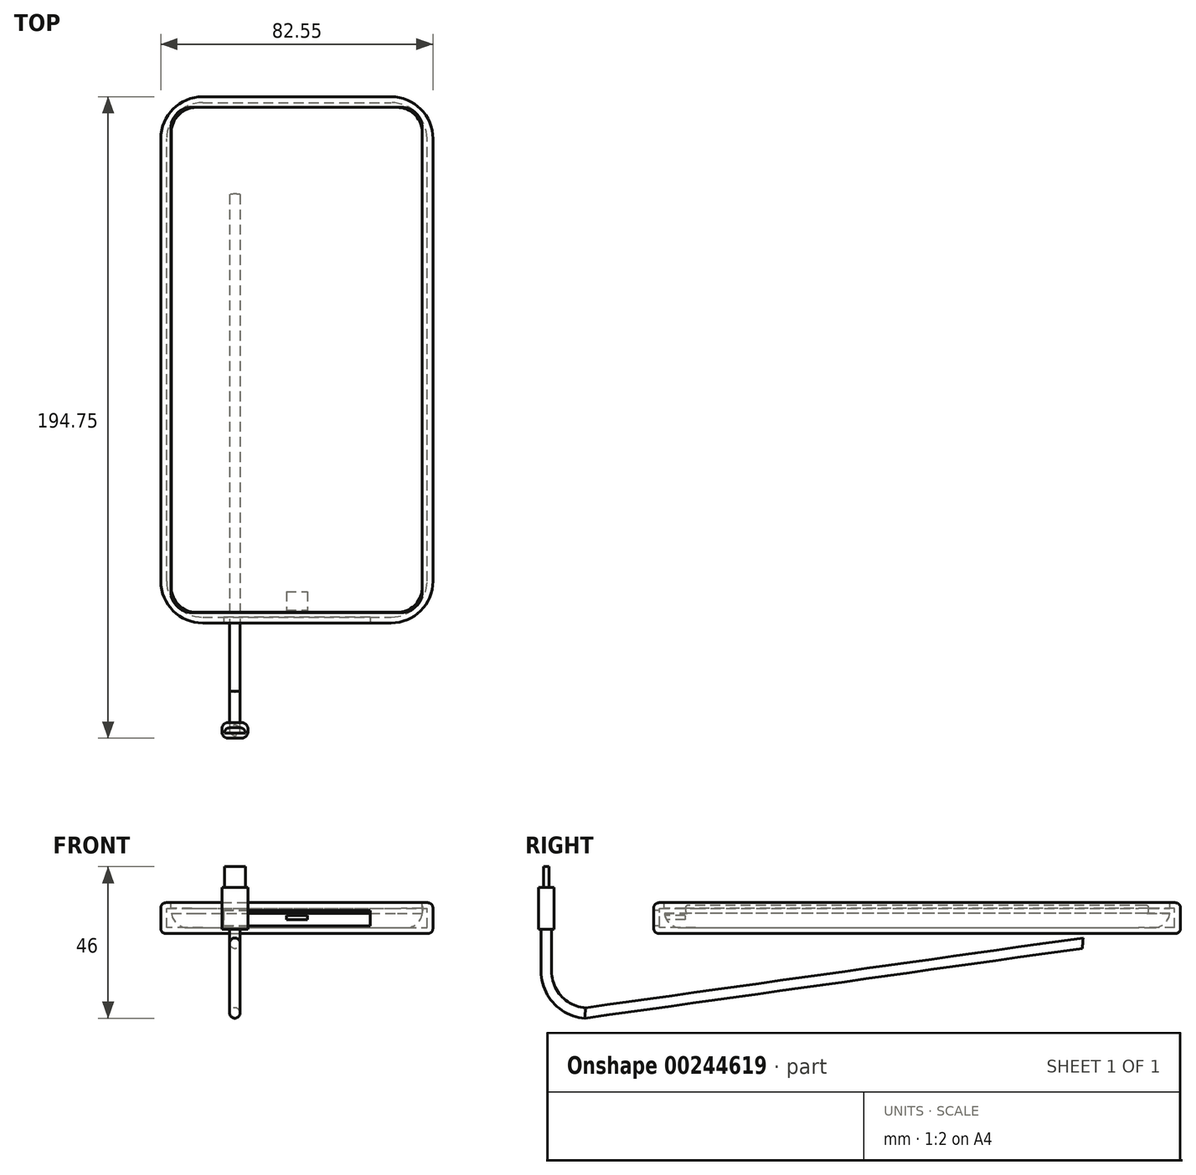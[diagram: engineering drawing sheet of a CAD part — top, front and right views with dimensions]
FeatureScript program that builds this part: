
annotation { "Feature Type Name" : "Feature", "Feature Type Description" : "" }
export const myFeature = defineFeature(function(context is Context, id is Id, definition is map)
    precondition{}
    {
        {
            var Q0;
            Q0=qCreatedBy(makeId("Top.planeOp"),FACE);
            var sketch = newSketch(context, id + "F0", { "sketchPlane" : qUnion([Q0])});
            skLineSegment(sketch, "E0.bottom", {"start": v(-19.3, -23.27) * mm, "end": v(56.9, -23.27) * mm});
            skLineSegment(sketch, "E0.top", {"start": v(-19.3, 130.15) * mm, "end": v(56.9, 130.15) * mm});
            skLineSegment(sketch, "E0.left", {"start": v(-19.3, -23.27) * mm, "end": v(-19.3, 130.15) * mm});
            skLineSegment(sketch, "E0.right", {"start": v(56.9, -23.27) * mm, "end": v(56.9, 130.15) * mm});
            skSolve(sketch);
        }
        {
            var Q0;
            Q0=makeQuery(id+"F0.imprint","IMPRINT",FACE,{"disambiguationData":[TD([[makeQuery(id+"F0.imprint","IMPRINT",EDGE,{"derivedFrom":sQuery(id+"F0.wireOp",EDGE,"E0.bottom")}),1.0]])]});
            extrude(context, id + "F1", {"entities" : qUnion([Q0]), "depth" : 7.62 * mm});
        }
        {
            var Q0;
            Q0=makeQuery(id+"F1.opExtrude","SWEPT_EDGE",EDGE,{"disambiguationData":[OSD([sQuery(id+"F0.wireOp",EDGE,"E0.bottom"),sQuery(id+"F0.wireOp",EDGE,"E0.left")])]});
            var Q1;
            Q1=makeQuery(id+"F1.opExtrude","SWEPT_EDGE",EDGE,{"disambiguationData":[OSD([sQuery(id+"F0.wireOp",EDGE,"E0.top"),sQuery(id+"F0.wireOp",EDGE,"E0.left")])]});
            var Q2;
            Q2=makeQuery(id+"F1.opExtrude","SWEPT_EDGE",EDGE,{"disambiguationData":[OSD([sQuery(id+"F0.wireOp",EDGE,"E0.top"),sQuery(id+"F0.wireOp",EDGE,"E0.right")])]});
            var Q3;
            Q3=makeQuery(id+"F1.opExtrude","SWEPT_EDGE",EDGE,{"disambiguationData":[OSD([sQuery(id+"F0.wireOp",EDGE,"E0.bottom"),sQuery(id+"F0.wireOp",EDGE,"E0.right")])]});
            fillet(context, id + "F2", {"entities" : qUnion([Q0, Q1, Q2, Q3]), "radius" : 7.62 * mm, "tangentPropagation" : true, "allowEdgeOverflow" : false});
        }
        {
            var Q0;
            Q0=makeQuery(id+"F1.opExtrude","CAP_EDGE",EDGE,{"disambiguationData":[OSD([sQuery(id+"F0.wireOp",EDGE,"E0.top")])],"isStart":true});
            var Q1;
            Q1=makeQuery(id+"F1.opExtrude","CAP_FACE",FACE,{"disambiguationData":[OSD([sQuery(id+"F0.wireOp",EDGE,"E0.bottom"),sQuery(id+"F0.wireOp",EDGE,"E0.top"),sQuery(id+"F0.wireOp",EDGE,"E0.left"),sQuery(id+"F0.wireOp",EDGE,"E0.right")])],"isStart":true});
            fillet(context, id + "F3", {"entities" : qUnion([Q0, Q1]), "radius" : 5.08 * mm, "tangentPropagation" : true, "allowEdgeOverflow" : false});
        }
        {
            var Q0;
            Q0=makeQuery(id+"F1.opExtrude","CAP_EDGE",EDGE,{"disambiguationData":[OSD([sQuery(id+"F0.wireOp",EDGE,"E0.top")])],"isStart":false});
            fillet(context, id + "F4", {"entities" : qUnion([Q0]), "radius" : 1.27 * mm, "tangentPropagation" : true, "allowEdgeOverflow" : false});
        }
        {
            var Q0;
            Q0=makeQuery(id+"F1.opExtrude","SWEPT_FACE",FACE,{"disambiguationData":[OSD([sQuery(id+"F0.wireOp",EDGE,"E0.bottom")])]});
            var sketch = newSketch(context, id + "F5", { "sketchPlane" : qUnion([Q0])});
            skLineSegment(sketch, "E1.bottom", {"start": v(15.62, 3.76) * mm, "end": v(21.97, 3.76) * mm});
            skLineSegment(sketch, "E1.top", {"start": v(15.62, 2.49) * mm, "end": v(21.97, 2.49) * mm});
            skLineSegment(sketch, "E1.left", {"start": v(15.62, 3.76) * mm, "end": v(15.62, 2.49) * mm});
            skLineSegment(sketch, "E1.right", {"start": v(21.97, 3.76) * mm, "end": v(21.97, 2.49) * mm});
            skSolve(sketch);
        }
        {
            var Q0;
            Q0=makeQuery(id+"F5.imprint","IMPRINT",FACE,{"disambiguationData":[TD([[makeQuery(id+"F5.imprint","IMPRINT",EDGE,{"derivedFrom":sQuery(id+"F5.wireOp",EDGE,"E1.bottom")}),-1.0]])]});
            extrude(context, id + "F6", {"entities" : qUnion([Q0]), "operationType" : NewBodyOperationType.REMOVE, "oppositeDirection" : true, "depth" : 6.35 * mm});
        }
        {
            var Q0;
            Q0=qCreatedBy(makeId("Right.planeOp"),FACE);
            var sketch = newSketch(context, id + "F7", { "sketchPlane" : qUnion([Q0])});
            skLineSegment(sketch, "E2", {"start": v(-59.05, -0.5) * mm, "end": v(-59.05, -13.2) * mm});
            skArc(sketch, "E3", {"start": v(-59.05, -13.2) * mm, "mid": v(-55.64, -21.86) * mm, "end": v(-47.24, -25.87) * mm});
            skLineSegment(sketch, "E4", {"start": v(-47.24, -25.87) * mm, "end": v(103.67, -4.66) * mm});
            skSolve(sketch);
        }
        {
            var Q0;
            Q0=sQuery(id+"F7.wireOp",VERTEX,"E2.start");
            var Q1;
            Q1=qCreatedBy(makeId("Top.planeOp"),FACE);
            cPlane(context, id + "F8", {"entities" : qUnion([Q0, Q1]), "cplaneType" : CPlaneType.PLANE_POINT, "offset" : 25.4 * mm, "width" : 152.4 * mm, "height" : 152.4 * mm});
        }
        {
            var Q0;
            Q0=qCreatedBy(id+"F8.planeOp",FACE);
            var sketch = newSketch(context, id + "F9", { "sketchPlane" : qUnion([Q0])});
            skCircle(sketch, "E5", {"center": v(0, -59.05) * mm, "radius": 1.59 * mm});
            skSolve(sketch);
        }
        {
            var Q0;
            Q0=makeQuery(id+"F9.imprint","IMPRINT",FACE,{"disambiguationData":[TD([[makeQuery(id+"F9.imprint","IMPRINT",EDGE,{"derivedFrom":sQuery(id+"F9.wireOp",EDGE,"E5")}),1.0]])]});
            var Q1;
            Q1=sQuery(id+"F7.wireOp",EDGE,"E2");
            sweep(context, id + "F10", {"profiles" : qUnion([Q0]), "path" : qUnion([Q1]), "keepProfileOrientation" : true});
        }
        {
            var Q0;
            Q0=makeQuery(id+"F10.opSweep","CAP_FACE",FACE,{"disambiguationData":[OSD([sQuery(id+"F7.wireOp",VERTEX,"E2.end"),sQuery(id+"F9.wireOp",EDGE,"E5")])],"isStart":false});
            var Q1;
            Q1=sQuery(id+"F7.wireOp",EDGE,"E3");
            sweep(context, id + "F11", {"operationType" : NewBodyOperationType.ADD, "profiles" : qUnion([Q0]), "path" : qUnion([Q1])});
        }
        {
            var Q0;
            Q0=makeQuery(id+"F11.opSweep","CAP_FACE",FACE,{"disambiguationData":[OSD([sQuery(id+"F7.wireOp",VERTEX,"E2.end"),sQuery(id+"F7.wireOp",VERTEX,"E3.end"),sQuery(id+"F9.wireOp",EDGE,"E5")])],"isStart":false});
            var Q1;
            Q1=sQuery(id+"F7.wireOp",EDGE,"E4");
            sweep(context, id + "F12", {"operationType" : NewBodyOperationType.ADD, "profiles" : qUnion([Q0]), "path" : qUnion([Q1])});
        }
        {
            var Q0;
            Q0=qCreatedBy(id+"F8.planeOp",FACE);
            var sketch = newSketch(context, id + "F13", { "sketchPlane" : qUnion([Q0])});
            skLineSegment(sketch, "E6.bottom", {"start": v(3.97, -56.66) * mm, "end": v(-3.97, -56.66) * mm});
            skLineSegment(sketch, "E6.top", {"start": v(3.97, -61.43) * mm, "end": v(-3.97, -61.43) * mm});
            skLineSegment(sketch, "E6.left", {"start": v(3.97, -56.66) * mm, "end": v(3.97, -61.43) * mm});
            skLineSegment(sketch, "E6.right", {"start": v(-3.97, -56.66) * mm, "end": v(-3.97, -61.43) * mm});
            skPoint(sketch, "E6.middle", {"position": v(0, -59.05) * mm});
            skSolve(sketch);
        }
        {
            var Q0;
            Q0=makeQuery(id+"F13.imprint","IMPRINT",FACE,{"disambiguationData":[TD([[makeQuery(id+"F13.imprint","IMPRINT",EDGE,{"derivedFrom":sQuery(id+"F13.wireOp",EDGE,"E6.bottom")}),1.0]])]});
            extrude(context, id + "F14", {"entities" : qUnion([Q0]), "operationType" : NewBodyOperationType.ADD, "depth" : 12.7 * mm});
        }
        {
            var Q0;
            Q0=makeQuery(id+"F14.opExtrude","SWEPT_EDGE",EDGE,{"disambiguationData":[OSD([sQuery(id+"F13.wireOp",EDGE,"E6.bottom"),sQuery(id+"F13.wireOp",EDGE,"E6.right")])]});
            var Q1;
            Q1=makeQuery(id+"F14.opExtrude","SWEPT_EDGE",EDGE,{"disambiguationData":[OSD([sQuery(id+"F13.wireOp",EDGE,"E6.top"),sQuery(id+"F13.wireOp",EDGE,"E6.right")])]});
            var Q2;
            Q2=makeQuery(id+"F14.opExtrude","SWEPT_EDGE",EDGE,{"disambiguationData":[OSD([sQuery(id+"F13.wireOp",EDGE,"E6.top"),sQuery(id+"F13.wireOp",EDGE,"E6.left")])]});
            var Q3;
            Q3=makeQuery(id+"F14.opExtrude","SWEPT_EDGE",EDGE,{"disambiguationData":[OSD([sQuery(id+"F13.wireOp",EDGE,"E6.bottom"),sQuery(id+"F13.wireOp",EDGE,"E6.left")])]});
            fillet(context, id + "F15", {"entities" : qUnion([Q0, Q1, Q2, Q3]), "radius" : 1.98 * mm, "tangentPropagation" : true, "allowEdgeOverflow" : false});
        }
        {
            var Q0;
            Q0=makeQuery(id+"F14.opExtrude","CAP_FACE",FACE,{"disambiguationData":[OSD([sQuery(id+"F13.wireOp",EDGE,"E6.bottom"),sQuery(id+"F13.wireOp",EDGE,"E6.top"),sQuery(id+"F13.wireOp",EDGE,"E6.left"),sQuery(id+"F13.wireOp",EDGE,"E6.right")])],"isStart":false});
            var sketch = newSketch(context, id + "F16", { "sketchPlane" : qUnion([Q0])});
            skLineSegment(sketch, "E7.bottom", {"start": v(-3.17, -58.25) * mm, "end": v(3.18, -58.25) * mm});
            skLineSegment(sketch, "E7.top", {"start": v(-3.18, -59.84) * mm, "end": v(3.18, -59.84) * mm});
            skLineSegment(sketch, "E7.left", {"start": v(-3.18, -58.25) * mm, "end": v(-3.18, -59.84) * mm});
            skLineSegment(sketch, "E7.right", {"start": v(3.18, -58.25) * mm, "end": v(3.18, -59.84) * mm});
            skPoint(sketch, "E7.middle", {"position": v(0, -59.05) * mm});
            skSolve(sketch);
        }
        {
            var Q0;
            Q0=qSketchRegion(id+"F16",true);
            extrude(context, id + "F17", {"entities" : qUnion([Q0]), "operationType" : NewBodyOperationType.ADD, "depth" : 6.35 * mm});
        }
        {
            var Q0;
            Q0=makeQuery(id+"F17.opExtrude","SWEPT_EDGE",EDGE,{"disambiguationData":[OSD([sQuery(id+"F16.wireOp",EDGE,"E7.bottom"),sQuery(id+"F16.wireOp",EDGE,"E7.right")])]});
            var Q1;
            Q1=makeQuery(id+"F17.opExtrude","SWEPT_EDGE",EDGE,{"disambiguationData":[OSD([sQuery(id+"F16.wireOp",EDGE,"E7.bottom"),sQuery(id+"F16.wireOp",EDGE,"E7.left")])]});
            fillet(context, id + "F18", {"entities" : qUnion([Q0, Q1]), "radius" : 1.59 * mm, "tangentPropagation" : true, "allowEdgeOverflow" : false});
        }
        {
            var Q0;
            Q0=qCreatedBy(makeId("Top.planeOp"),FACE);
            var sketch = newSketch(context, id + "F19", { "sketchPlane" : qUnion([Q0])});
            skLineSegment(sketch, "E8.bottom", {"start": v(-22.48, -26.45) * mm, "end": v(60.07, -26.45) * mm});
            skLineSegment(sketch, "E8.top", {"start": v(-22.48, 133.32) * mm, "end": v(60.07, 133.32) * mm});
            skLineSegment(sketch, "E8.left", {"start": v(-22.48, -26.45) * mm, "end": v(-22.48, 133.32) * mm});
            skLineSegment(sketch, "E8.right", {"start": v(60.07, -26.45) * mm, "end": v(60.07, 133.32) * mm});
            skSolve(sketch);
        }
        {
            var Q0;
            Q0=makeQuery(id+"F19.imprint","IMPRINT",FACE,{"disambiguationData":[TD([[makeQuery(id+"F19.imprint","IMPRINT",EDGE,{"derivedFrom":sQuery(id+"F19.wireOp",EDGE,"E8.bottom")}),1.0]])]});
            extrude(context, id + "F20", {"entities" : qUnion([Q0]), "depth" : 9.4 * mm});
        }
        {
            var Q0;
            Q0=makeQuery(id+"F20.opExtrude","SWEPT_EDGE",EDGE,{"disambiguationData":[OSD([sQuery(id+"F19.wireOp",EDGE,"E8.top"),sQuery(id+"F19.wireOp",EDGE,"E8.left")])]});
            var Q1;
            Q1=makeQuery(id+"F20.opExtrude","SWEPT_EDGE",EDGE,{"disambiguationData":[OSD([sQuery(id+"F19.wireOp",EDGE,"E8.bottom"),sQuery(id+"F19.wireOp",EDGE,"E8.left")])]});
            var Q2;
            Q2=makeQuery(id+"F20.opExtrude","SWEPT_EDGE",EDGE,{"disambiguationData":[OSD([sQuery(id+"F19.wireOp",EDGE,"E8.bottom"),sQuery(id+"F19.wireOp",EDGE,"E8.right")])]});
            var Q3;
            Q3=makeQuery(id+"F20.opExtrude","SWEPT_EDGE",EDGE,{"disambiguationData":[OSD([sQuery(id+"F19.wireOp",EDGE,"E8.top"),sQuery(id+"F19.wireOp",EDGE,"E8.right")])]});
            fillet(context, id + "F21", {"entities" : qUnion([Q0, Q1, Q2, Q3]), "radius" : 12.7 * mm, "tangentPropagation" : true, "allowEdgeOverflow" : false});
        }
        {
            var Q0;
            Q0=makeQuery(id+"F20.opExtrude","CAP_FACE",FACE,{"disambiguationData":[OSD([sQuery(id+"F19.wireOp",EDGE,"E8.bottom"),sQuery(id+"F19.wireOp",EDGE,"E8.top"),sQuery(id+"F19.wireOp",EDGE,"E8.left"),sQuery(id+"F19.wireOp",EDGE,"E8.right")])],"isStart":false});
            var Q1;
            Q1=makeQuery(id+"F20.opExtrude","SWEPT_BODY",BODY,{"disambiguationData":[OSD([sQuery(id+"F19.wireOp",EDGE,"E8.bottom"),sQuery(id+"F19.wireOp",EDGE,"E8.top"),sQuery(id+"F19.wireOp",EDGE,"E8.left"),sQuery(id+"F19.wireOp",EDGE,"E8.right")])]});
            shell(context, id + "F22", {"isHollow" : true, "entities" : qUnion([Q0]), "parts" : qUnion([Q1]), "thickness" : 1.78 * mm});
        }
        {
            var Q0;
            Q0=makeQuery(id+"F20.opExtrude","CAP_FACE",FACE,{"disambiguationData":[OSD([sQuery(id+"F19.wireOp",EDGE,"E8.bottom"),sQuery(id+"F19.wireOp",EDGE,"E8.top"),sQuery(id+"F19.wireOp",EDGE,"E8.left"),sQuery(id+"F19.wireOp",EDGE,"E8.right")])],"isStart":false});
            var sketch = newSketch(context, id + "F23", { "sketchPlane" : qUnion([Q0])});
            skLineSegment(sketch, "E9.bottom", {"start": v(-13.04, 130.15) * mm, "end": v(50.46, 130.15) * mm});
            skLineSegment(sketch, "E9.top", {"start": v(-13.04, -23.27) * mm, "end": v(50.46, -23.27) * mm});
            skLineSegment(sketch, "E9.left", {"start": v(-19.39, 123.8) * mm, "end": v(-19.39, -16.92) * mm});
            skLineSegment(sketch, "E9.right", {"start": v(56.81, 123.8) * mm, "end": v(56.81, -16.92) * mm});
            skPoint(sketch, "E9.middle", {"position": v(-17.36, 110.44) * mm});
            skPoint(sketch, "E10.visualSharp", {"position": v(-55.46, 193.5) * mm});
            skArc(sketch, "E10.filletArc", {"start": v(-13.04, 130.15) * mm, "mid": v(-17.53, 128.29) * mm, "end": v(-19.39, 123.8) * mm});
            skPoint(sketch, "E11.visualSharp", {"position": v(20.74, 193.5) * mm});
            skArc(sketch, "E11.filletArc", {"start": v(56.81, 123.8) * mm, "mid": v(54.95, 128.29) * mm, "end": v(50.46, 130.15) * mm});
            skPoint(sketch, "E12.visualSharp", {"position": v(20.74, 33.73) * mm});
            skArc(sketch, "E12.filletArc", {"start": v(50.46, -23.27) * mm, "mid": v(54.95, -21.41) * mm, "end": v(56.81, -16.92) * mm});
            skPoint(sketch, "E13.visualSharp", {"position": v(-55.46, 33.73) * mm});
            skArc(sketch, "E13.filletArc", {"start": v(-19.39, -16.92) * mm, "mid": v(-17.53, -21.41) * mm, "end": v(-13.04, -23.27) * mm});
            skSolve(sketch);
        }
        {
            var Q0;
            Q0=qSketchRegion(id+"F23",true);
            extrude(context, id + "F24", {"entities" : qUnion([Q0]), "operationType" : NewBodyOperationType.REMOVE, "oppositeDirection" : true, "depth" : 5.08 * mm});
        }
        {
            var Q0;
            Q0=makeQuery(id+"F20.opExtrude","SWEPT_FACE",FACE,{"disambiguationData":[OSD([sQuery(id+"F19.wireOp",EDGE,"E8.bottom")])]});
            var sketch = newSketch(context, id + "F25", { "sketchPlane" : qUnion([Q0])});
            skLineSegment(sketch, "E14.bottom", {"start": v(-3.43, 7.08) * mm, "end": v(41.02, 7.08) * mm});
            skLineSegment(sketch, "E14.top", {"start": v(-3.43, 2.32) * mm, "end": v(41.02, 2.32) * mm});
            skLineSegment(sketch, "E14.left", {"start": v(-3.43, 7.08) * mm, "end": v(-3.43, 2.32) * mm});
            skLineSegment(sketch, "E14.right", {"start": v(41.02, 7.08) * mm, "end": v(41.02, 2.32) * mm});
            skPoint(sketch, "E14.middle", {"position": v(18.8, 4.7) * mm});
            skSolve(sketch);
        }
        {
            var Q0;
            Q0=makeQuery(id+"F25.imprint","IMPRINT",FACE,{"disambiguationData":[TD([[makeQuery(id+"F25.imprint","IMPRINT",EDGE,{"derivedFrom":sQuery(id+"F25.wireOp",EDGE,"E14.bottom")}),-1.0]])]});
            extrude(context, id + "F26", {"entities" : qUnion([Q0]), "operationType" : NewBodyOperationType.REMOVE, "oppositeDirection" : true, "depth" : 1.9 * mm});
        }
        {
            var Q0;
            Q0=makeQuery(id+"F20.opExtrude","SWEPT_BODY",BODY,{"disambiguationData":[OSD([sQuery(id+"F19.wireOp",EDGE,"E8.bottom"),sQuery(id+"F19.wireOp",EDGE,"E8.top"),sQuery(id+"F19.wireOp",EDGE,"E8.left"),sQuery(id+"F19.wireOp",EDGE,"E8.right")])]});
            transform(context, id + "F27", {"entities" : qUnion([Q0]), "transformType" : TransformType.TRANSLATION_3D, "dx" : 0 * mm, "dy" : 0 * mm, "dz" : -1.78 * mm, "makeCopy" : false});
        }
        {
            var Q0;
            Q0=makeQuery(id+"F20.opExtrude","CAP_EDGE",EDGE,{"disambiguationData":[OSD([sQuery(id+"F19.wireOp",EDGE,"E8.left")])],"isStart":false});
            var Q1;
            Q1=makeQuery(id+"F20.opExtrude","CAP_EDGE",EDGE,{"disambiguationData":[OSD([sQuery(id+"F19.wireOp",EDGE,"E8.left")])],"isStart":true});
            fillet(context, id + "F28", {"entities" : qUnion([Q0, Q1]), "radius" : 1.59 * mm, "tangentPropagation" : true, "allowEdgeOverflow" : false});
        }
    });
